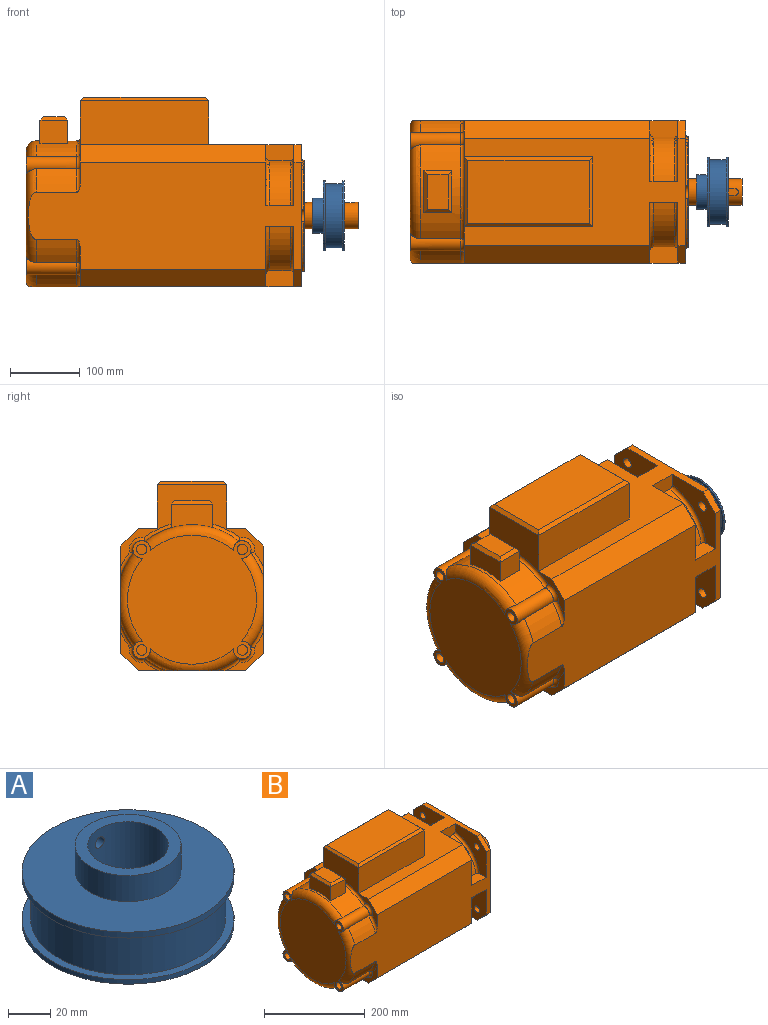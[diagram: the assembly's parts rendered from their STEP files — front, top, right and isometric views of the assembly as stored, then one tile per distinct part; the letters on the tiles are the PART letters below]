
ASSEMBLY  parts=2 mates=1
PART A: 13 faces, bbox 100x100x45 mm
  f0: plane 100x100mm, normal (0,0,1), area 5890.5mm2, adj f1,f11
  f1: cylinder r=25mm len=50mm, axis (0,0,1), area 2327.9mm2, adj f0,f2,f12
  f2: plane 50x50mm, normal (0,0,1), area 829.4mm2, adj f1,f3
  f3: cylinder r=19mm len=38mm, axis (0,0,1), area 3553mm2, adj f2,f4,f12
  f4: plane 40x40mm, normal (0,0,-1), area 122.5mm2, adj f3,f5
  f5: cylinder r=20mm len=40mm, axis (0,0,1), area 1885mm2, adj f4,f6
  f6: plane 100x100mm, normal (0,0,-1), area 6597.3mm2, adj f5,f7
  f7: cylinder r=50mm len=100mm, axis (0,0,1), area 819.2mm2, adj f6,f8
  f8: plane 100x100mm, normal (0,0,1), area 1206.4mm2, adj f7,f9
  f9: cylinder r=46mm len=92mm, axis (0,0,1), area 6940mm2, adj f8,f10
  f10: plane 100x100mm, normal (0,0,-1), area 1206.4mm2, adj f9,f11
  f11: cylinder r=50mm len=100mm, axis (0,0,1), area 1062.1mm2, adj f0,f10
  f12: cylinder r=3mm len=6.24mm, axis (0,-1,0), area 113.6mm2, adj f1,f3
PART B: 142 faces, bbox 478.4x235.1x288.7 mm
  f0: cylinder r=12.5mm len=73mm, axis (1,0,0), area 2236.6mm2, adj f1,f2,f3,f13,f14,f17
  f1: plane 185x185mm, normal (-1,0,0), area 28010.6mm2, adj f0,f2,f3,f4,f5,f6,f7,f8
  f2: torus R=92.5mm, axis (1,0,0), area 2522.2mm2, adj f0,f1,f8,f13,f15,f16
  f3: torus R=92.5mm, axis (1,0,0), area 2522.1mm2, adj f0,f1,f4,f17,f18,f19
  f4: cylinder r=12.5mm len=73mm, axis (1,0,0), area 2236.8mm2, adj f1,f3,f5,f19,f20,f21
  f5: torus R=92.5mm, axis (1,0,0), area 3230.5mm2, adj f1,f4,f6,f21
  f6: cylinder r=12.5mm len=73mm, axis (1,0,0), area 2236.6mm2, adj f1,f5,f7,f21,f22,f23
  f7: torus R=92.5mm, axis (1,0,0), area 2522.1mm2, adj f1,f6,f8,f23,f24,f25
  f8: cylinder r=12.5mm len=73mm, axis (1,0,0), area 2236.8mm2, adj f1,f2,f7,f15,f25,f26
  f9: cylinder r=7.5mm len=92mm, axis (1,0,0), area 4335.4mm2, adj f1,f27
  f10: cylinder r=7.5mm len=92mm, axis (1,0,0), area 4335.4mm2, adj f1,f28
  f11: cylinder r=7.5mm len=92mm, axis (1,0,0), area 4335.4mm2, adj f1,f29
  f12: cylinder r=7.5mm len=92mm, axis (1,0,0), area 4335.4mm2, adj f1,f30
  f13: cylinder r=107.5mm len=58mm, axis (1,0,0), area 2225.2mm2, adj f0,f2,f16,f31
  f14: torus R=17.5mm, axis (1,0,0), area 242.1mm2, adj f0,f31,f32,f33
  f15: cylinder r=107.5mm len=58mm, axis (1,0,0), area 2225.2mm2, adj f2,f8,f16,f34
  f16: plane 393.98x156.37mm, normal (0,0,-1), area 48804.2mm2, adj f2,f13,f15,f31,f32,f34,f35,f36
  f17: cylinder r=107.5mm len=58mm, axis (1,0,0), area 2225.2mm2, adj f0,f3,f18,f33
  f18: plane 393.98x156.37mm, normal (0,1,0), area 48800.8mm2, adj f3,f17,f19,f32,f33,f35,f36,f38
  f19: cylinder r=107.5mm len=58mm, axis (1,0,0), area 2225.2mm2, adj f3,f4,f18,f44
  f20: torus R=17.5mm, axis (1,0,0), area 242.1mm2, adj f4,f44,f50,f51
  f21: cylinder r=107.5mm len=134.88mm, axis (1,0,0), area 6024.2mm2, adj f4,f5,f6,f51,f52,f53,f54,f55
  f22: torus R=17.5mm, axis (1,0,0), area 242.1mm2, adj f6,f50,f51,f56
  f23: cylinder r=107.5mm len=58mm, axis (1,0,0), area 2225.2mm2, adj f6,f7,f24,f56
  f24: plane 393.98x156.37mm, normal (0,-1,0), area 48800.4mm2, adj f7,f23,f25,f39,f41,f42,f43,f50
  f25: cylinder r=107.5mm len=58mm, axis (1,0,0), area 2225.2mm2, adj f7,f8,f24,f62
  f26: torus R=17.5mm, axis (1,0,0), area 242.1mm2, adj f8,f34,f43,f62
  f27: plane 15x15mm, normal (-1,0,0), area 176.7mm2, adj f9
  f28: plane 15x15mm, normal (-1,0,0), area 176.7mm2, adj f10
  f29: plane 15x15mm, normal (-1,0,0), area 176.7mm2, adj f11
  f30: plane 15x15mm, normal (-1,0,0), area 176.7mm2, adj f12
  f31: torus R=112.5mm, axis (1,0,0), area 246.8mm2, adj f13,f14,f16,f32
  f32: plane 54.54x54.54mm, normal (-1,0,0), area 676.4mm2, adj f14,f16,f18,f31,f33,f35
  f33: torus R=112.5mm, axis (1,0,0), area 246.8mm2, adj f14,f17,f18,f32
  f34: torus R=112.5mm, axis (1,0,0), area 246.8mm2, adj f15,f16,f26,f43
  f35: plane 266x25mm, normal (0,0.71,-0.71), area 9404.5mm2, adj f16,f18,f32,f36
  f36: plane 87x87mm, normal (1,0,0), area 3893.7mm2, adj f16,f18,f35,f37,f45,f63
  f37: plane 40.36x23.78mm, normal (0,1,0), area 925.8mm2, adj f16,f36,f63,f64,f65,f133
  f38: plane 25x25mm, normal (0,0.71,-0.71), area 388.9mm2, adj f16,f18,f129,f133
  f39: plane 25x25mm, normal (0,-0.71,-0.71), area 388.9mm2, adj f16,f24,f129,f130
  f40: plane 40.36x23.78mm, normal (0,-1,0), area 925.8mm2, adj f16,f41,f75,f76,f77,f130
  f41: plane 87x87mm, normal (1,0,0), area 3893.7mm2, adj f16,f24,f40,f42,f61,f77
  f42: plane 266x25mm, normal (0,-0.71,-0.71), area 9404.5mm2, adj f16,f24,f41,f43
  f43: plane 54.54x54.54mm, normal (-1,0,0), area 676.4mm2, adj f16,f24,f26,f34,f42,f62
  f44: torus R=112.5mm, axis (1,0,0), area 246.8mm2, adj f18,f19,f20,f50
  f45: plane 40.36x23.78mm, normal (0,0,-1), area 925.8mm2, adj f18,f36,f63,f64,f65,f133
  f46: plane 25x25mm, normal (0,0.71,0.71), area 388.9mm2, adj f18,f66,f129,f131
  f47: plane 40.36x23.78mm, normal (0,0,1), area 925.8mm2, adj f18,f48,f79,f80,f81,f131
  f48: plane 87x87mm, normal (1,0,0), area 3893.7mm2, adj f18,f47,f49,f66,f78,f80
  f49: plane 266x25mm, normal (0,0.71,0.71), area 9404.5mm2, adj f18,f48,f50,f66
  f50: plane 204x117.54mm, normal (-1,0,0), area 6982mm2, adj f18,f20,f22,f24,f44,f49,f51,f56
  f51: torus R=112.5mm, axis (1,0,0), area 1144.1mm2, adj f20,f21,f22,f50
  f52: plane 60x33.77mm, normal (1,0,0), area 1854.7mm2, adj f21,f53,f55,f85
  f53: plane 40x33.77mm, normal (0,-1,0), area 1350.8mm2, adj f21,f52,f54,f86
  f54: plane 60x33.77mm, normal (-1,0,0), area 1854.7mm2, adj f21,f53,f55,f87
  f55: plane 40x33.77mm, normal (0,1,0), area 1272.3mm2, adj f21,f52,f54,f88,f89
  f56: torus R=112.5mm, axis (1,0,0), area 246.8mm2, adj f22,f23,f24,f50
  f57: plane 266x25mm, normal (0,-0.71,0.71), area 9404.5mm2, adj f24,f50,f58,f66
  f58: plane 87x87mm, normal (1,0,0), area 3893.7mm2, adj f24,f57,f59,f66,f90,f91
  f59: plane 40.36x23.78mm, normal (0,0,1), area 925.8mm2, adj f24,f58,f91,f92,f93,f132
  f60: plane 25x25mm, normal (0,-0.71,0.71), area 388.9mm2, adj f24,f66,f129,f132
  f61: plane 40.36x23.78mm, normal (0,0,-1), area 925.8mm2, adj f24,f41,f75,f76,f77,f130
  f62: torus R=112.5mm, axis (1,0,0), area 246.8mm2, adj f24,f25,f26,f43
  f63: torus R=85mm, axis (1,0,0), area 774.3mm2, adj f36,f37,f45,f64
  f64: cylinder r=80mm len=63.58mm, axis (1,0,0), area 2864.6mm2, adj f37,f45,f63,f65
  f65: torus R=85mm, axis (1,0,0), area 774.3mm2, adj f37,f45,f64,f133
  f66: plane 317x154mm, normal (0,0,1), area 25458mm2, adj f46,f48,f49,f50,f57,f58,f60,f78
  f67: cylinder r=9mm len=55mm, axis (1,0,0), area 2996.9mm2, adj f68,f74,f95,f96,f97,f98,f129
  f68: torus R=83mm, axis (1,0,0), area 516.9mm2, adj f67,f69,f98,f129
  f69: cylinder r=9mm len=55mm, axis (1,0,0), area 2998.7mm2, adj f68,f70,f96,f98,f99,f100,f129
  f70: torus R=83mm, axis (1,0,0), area 516.9mm2, adj f69,f71,f100,f129
  f71: cylinder r=9mm len=55mm, axis (1,0,0), area 2996.9mm2, adj f70,f72,f96,f100,f101,f102,f129
  f72: torus R=83mm, axis (1,0,0), area 516.9mm2, adj f71,f73,f102,f129
  f73: cylinder r=9mm len=55mm, axis (1,0,0), area 2998.7mm2, adj f72,f74,f96,f97,f102,f103,f129
  f74: torus R=83mm, axis (1,0,0), area 516.9mm2, adj f67,f73,f97,f129
  f75: torus R=85mm, axis (1,0,0), area 774.3mm2, adj f40,f61,f76,f130
  f76: cylinder r=80mm len=63.58mm, axis (1,0,0), area 2864.6mm2, adj f40,f61,f75,f77
  f77: torus R=85mm, axis (1,0,0), area 774.3mm2, adj f40,f41,f61,f76
  f78: plane 40.36x23.78mm, normal (0,1,0), area 925.8mm2, adj f48,f66,f79,f80,f81,f131
  f79: torus R=85mm, axis (1,0,0), area 774.3mm2, adj f47,f78,f81,f131
  f80: torus R=85mm, axis (1,0,0), area 774.3mm2, adj f47,f48,f78,f81
  f81: cylinder r=80mm len=63.58mm, axis (1,0,0), area 2864.6mm2, adj f47,f78,f79,f80
  f82: plane 184x63mm, normal (0,1,0), area 9078.7mm2, adj f50,f66,f94,f104,f105,f106
  f83: plane 100x5mm, normal (-0.71,0,0.71), area 671.8mm2, adj f50,f104,f107,f108
  f84: plane 184x63mm, normal (0,-1,0), area 11592mm2, adj f50,f66,f94,f107
  f85: plane 60x5mm, normal (0.71,0,0.71), area 388.9mm2, adj f52,f86,f88,f109
  f86: plane 40x5mm, normal (0,-0.71,0.71), area 247.5mm2, adj f53,f85,f87,f109
  f87: plane 60x5mm, normal (-0.71,0,0.71), area 388.9mm2, adj f54,f86,f88,f109
  f88: plane 40x5mm, normal (0,0.71,0.71), area 247.5mm2, adj f55,f85,f87,f109
  f89: cylinder r=5mm len=40mm, axis (0,-1,0), area 1256.6mm2, adj f55,f110
  f90: plane 40.36x23.78mm, normal (0,-1,0), area 925.8mm2, adj f58,f66,f91,f92,f93,f132
  f91: torus R=85mm, axis (1,0,0), area 774.3mm2, adj f58,f59,f90,f92
  f92: cylinder r=80mm len=63.58mm, axis (1,0,0), area 2864.6mm2, adj f59,f90,f91,f93
  f93: torus R=85mm, axis (1,0,0), area 774.3mm2, adj f59,f90,f92,f132
  f94: plane 100x63mm, normal (1,0,0), area 6300mm2, adj f66,f82,f84,f111
  f95: plane 18x18mm, normal (1,0,0), area 254.5mm2, adj f67
  f96: plane 158.99x158.99mm, normal (1,0,0), area 4215.6mm2, adj f67,f69,f71,f73,f97,f98,f100,f102
  f97: cylinder r=80mm len=70.51mm, axis (1,0,0), area 107.7mm2, adj f67,f73,f74,f96
  f98: cylinder r=80mm len=70.51mm, axis (1,0,0), area 107.7mm2, adj f67,f68,f69,f96
  f99: plane 18x18mm, normal (1,0,0), area 254.5mm2, adj f69
  f100: cylinder r=80mm len=70.51mm, axis (1,0,0), area 107.7mm2, adj f69,f70,f71,f96
  f101: plane 18x18mm, normal (1,0,0), area 254.5mm2, adj f71
  f102: cylinder r=80mm len=70.51mm, axis (1,0,0), area 107.7mm2, adj f71,f72,f73,f96
  f103: plane 18x18mm, normal (1,0,0), area 254.5mm2, adj f73
  f104: plane 184x5mm, normal (0,0.71,0.71), area 1265.7mm2, adj f82,f83,f108,f111
  f105: cylinder r=20mm len=50mm, axis (0,-1,0), area 6283.2mm2, adj f82,f113
  f106: cylinder r=20mm len=50mm, axis (0,-1,0), area 6283.2mm2, adj f82,f114
  f107: plane 184x5mm, normal (0,-0.71,0.71), area 1265.7mm2, adj f83,f84,f108,f111
  f108: plane 174x90mm, normal (0,0,1), area 15660mm2, adj f83,f104,f107,f111
  f109: plane 50x30mm, normal (0,0,1), area 1500mm2, adj f85,f86,f87,f88
  f110: plane 10x10mm, normal (0,1,0), area 78.5mm2, adj f89
  f111: plane 100x5mm, normal (0.71,0,0.71), area 671.8mm2, adj f94,f104,f107,f108
  f112: cylinder r=70mm len=140mm, axis (1,0,0), area 879.6mm2, adj f96,f115
  f113: plane 40x40mm, normal (0,1,0), area 1256.6mm2, adj f105
  f114: plane 40x40mm, normal (0,1,0), area 1256.6mm2, adj f106
  f115: torus R=67mm, axis (1,0,0), area 2040.3mm2, adj f112,f116
  f116: plane 134x134mm, normal (1,0,0), area 6864.4mm2, adj f115,f117
  f117: torus R=48mm, axis (1,0,0), area 1364.7mm2, adj f116,f118
  f118: cylinder r=45mm len=90mm, axis (1,0,0), area 565.5mm2, adj f117,f119
  f119: plane 90x90mm, normal (1,0,0), area 5227.6mm2, adj f118,f120
  f120: cylinder r=19mm len=77mm, axis (1,0,0), area 8635.7mm2, adj f119,f121,f122,f123,f124,f125
  f121: plane 38x38mm, normal (1,0,0), area 1053.9mm2, adj f120,f126
  f122: cylinder r=5mm len=10mm, axis (0,0,1), area 84.3mm2, adj f120,f123,f125,f127
  f123: plane 50x5.03mm, normal (0,1,0), area 251.5mm2, adj f120,f122,f124,f127
  f124: cylinder r=5mm len=10mm, axis (0,0,1), area 84.3mm2, adj f120,f123,f125,f127
  f125: plane 50x5.03mm, normal (0,-1,0), area 251.5mm2, adj f120,f122,f124,f127
  f126: cylinder r=5.05mm len=35mm, axis (-1,0,0), area 1111.2mm2, adj f121,f128
  f127: plane 60x10mm, normal (0,0,1), area 578.5mm2, adj f122,f123,f124,f125
  f128: cone r=1.73mm half-angle=60deg, axis (1,0,0), area 92.6mm2, adj f126
  f129: plane 204x204mm, normal (1,0,0), area 17709.6mm2, adj f16,f18,f24,f38,f39,f46,f60,f66
  f130: plane 87x87mm, normal (-1,0,0), area 3717mm2, adj f16,f24,f39,f40,f61,f75,f135
  f131: plane 87x87mm, normal (-1,0,0), area 3717mm2, adj f18,f46,f47,f66,f78,f79,f136
  f132: plane 87x87mm, normal (-1,0,0), area 3717mm2, adj f24,f59,f60,f66,f90,f93,f134
  f133: plane 87x87mm, normal (-1,0,0), area 3717mm2, adj f16,f18,f37,f38,f45,f65,f137
  f134: cylinder r=7.5mm len=15mm, axis (1,0,0), area 518.4mm2, adj f129,f132
  f135: cylinder r=7.5mm len=15mm, axis (1,0,0), area 518.4mm2, adj f129,f130
  f136: cylinder r=7.5mm len=15mm, axis (1,0,0), area 518.4mm2, adj f129,f131
  f137: cylinder r=7.5mm len=15mm, axis (1,0,0), area 518.4mm2, adj f129,f133
  f138: cylinder r=78.58mm len=184mm, axis (1,0,0), area 90848.2mm2, adj f139,f140
  f139: plane 157.59x157.59mm, normal (-1,0,0), area 106.6mm2, adj f138,f141
  f140: plane 157.16x157.16mm, normal (-1,0,0), area 19399.3mm2, adj f138
  f141: revolved ~157.59x157.59mm, area 26887.5mm2, adj f139
PLACE A rot(axis=(0,-1,0),90deg) t=(-210.3,-168.42,71.31)mm
PLACE B t=(-252.3,-168.42,71.31)mm fixed
MATE fastened B.f34 <-> A.f1  axis (1,0,0) through (-175.3,-168.42,71.31)mm
